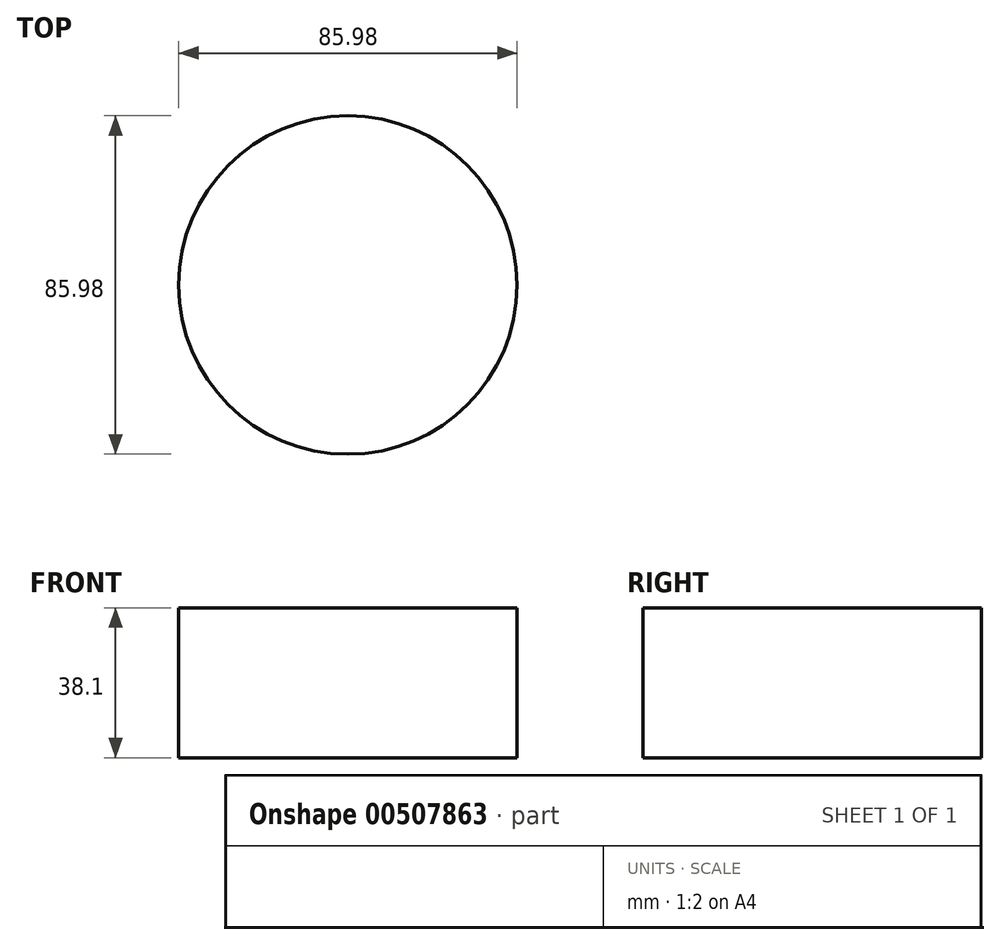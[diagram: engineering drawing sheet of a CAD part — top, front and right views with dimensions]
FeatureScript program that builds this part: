
annotation { "Feature Type Name" : "Feature", "Feature Type Description" : "" }
export const myFeature = defineFeature(function(context is Context, id is Id, definition is map)
    precondition{}
    {
        {
            var Q0;
            Q0=qCreatedBy(makeId("Top.planeOp"),FACE);
            var sketch = newSketch(context, id + "F0", { "sketchPlane" : qUnion([Q0])});
            skCircle(sketch, "E0", {"center": v(0, 0) * mm, "radius": 42.99 * mm});
            skSolve(sketch);
        }
        {
            var Q0;
            Q0 = qSketchRegion(id + "F0", true);
            extrude(context, id + "F1", {"entities" : qUnion([Q0]), "depth" : 38.1 * mm});
        }
    });
